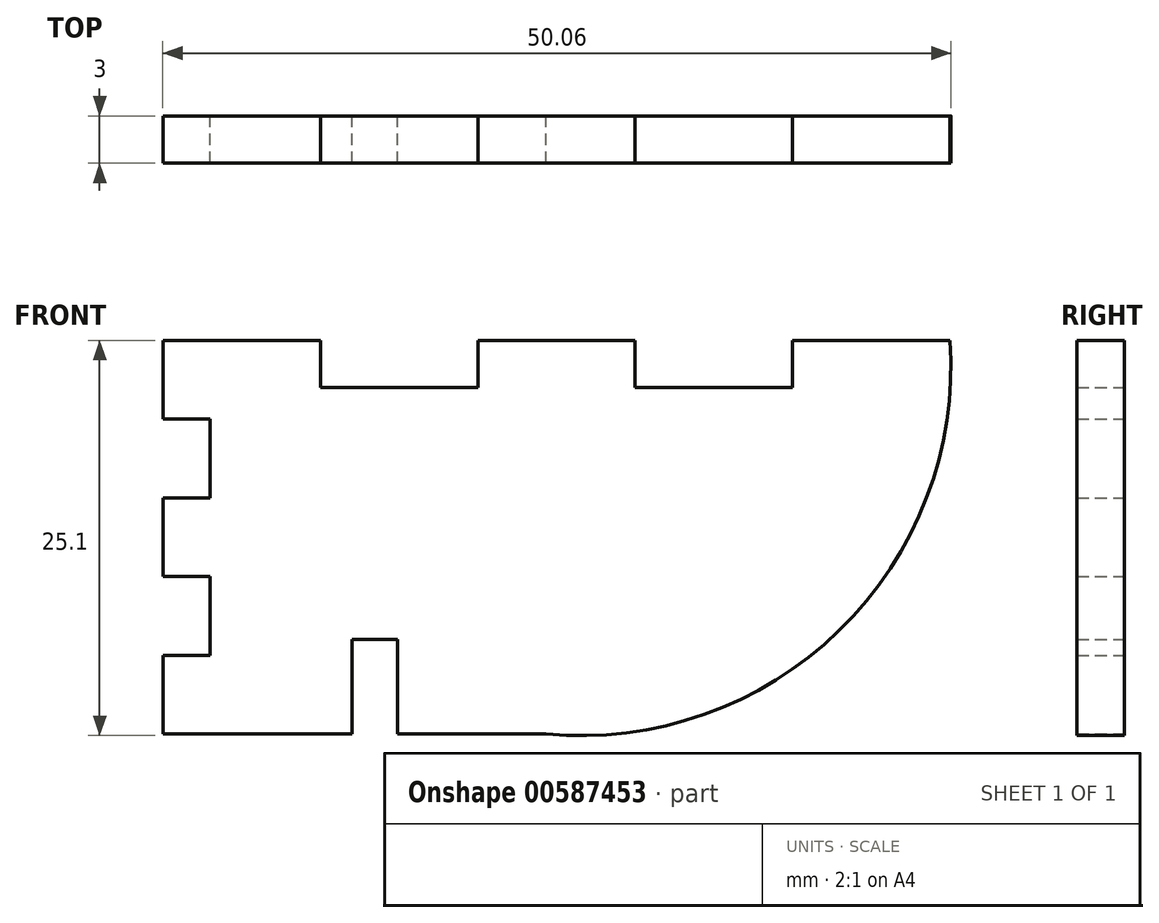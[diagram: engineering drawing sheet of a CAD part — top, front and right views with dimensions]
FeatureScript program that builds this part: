
annotation { "Feature Type Name" : "Feature", "Feature Type Description" : "" }
export const myFeature = defineFeature(function(context is Context, id is Id, definition is map)
    precondition{}
    {
        {
            var Q0;
            Q0=qCreatedBy(makeId("Front.planeOp"),FACE);
            var sketch = newSketch(context, id + "F0", { "sketchPlane" : qUnion([Q0])});
            skLineSegment(sketch, "E0", {"start": v(-35.85, 20) * mm, "end": v(-35.85, -5) * mm, "construction": true});
            skArc(sketch, "E1", {"start": v(-11.5, -5) * mm, "mid": v(7.1, 1.56) * mm, "end": v(14.15, 20) * mm});
            skLineSegment(sketch, "E2", {"start": v(-23.85, -5) * mm, "end": v(-23.85, 1) * mm});
            skLineSegment(sketch, "E3", {"start": v(-23.85, 1) * mm, "end": v(-20.95, 1) * mm});
            skLineSegment(sketch, "E4", {"start": v(-20.95, 1) * mm, "end": v(-20.95, -5) * mm});
            skLineSegment(sketch, "E5", {"start": v(-20.95, -5) * mm, "end": v(-11.5, -5) * mm});
            skLineSegment(sketch, "E6", {"start": v(-23.85, -5) * mm, "end": v(-35.85, -5) * mm});
            skLineSegment(sketch, "E7", {"start": v(-35.85, 0) * mm, "end": v(-32.85, 0) * mm});
            skLineSegment(sketch, "E8", {"start": v(-32.85, 0) * mm, "end": v(-32.85, 5) * mm});
            skLineSegment(sketch, "E9", {"start": v(-32.85, 5) * mm, "end": v(-35.85, 5) * mm});
            skLineSegment(sketch, "E10", {"start": v(-35.85, 5) * mm, "end": v(-35.85, 10) * mm});
            skLineSegment(sketch, "E11", {"start": v(-35.85, 10) * mm, "end": v(-32.85, 10) * mm});
            skLineSegment(sketch, "E12", {"start": v(-32.85, 10) * mm, "end": v(-32.85, 15) * mm});
            skLineSegment(sketch, "E13", {"start": v(-32.85, 15) * mm, "end": v(-35.85, 15) * mm});
            skLineSegment(sketch, "E14", {"start": v(-35.85, 15) * mm, "end": v(-35.85, 20) * mm});
            skLineSegment(sketch, "E15", {"start": v(-35.85, 0) * mm, "end": v(-35.85, -5) * mm});
            skLineSegment(sketch, "E16", {"start": v(-35.85, 20) * mm, "end": v(-25.85, 20) * mm});
            skLineSegment(sketch, "E17", {"start": v(-25.85, 20) * mm, "end": v(-25.85, 17) * mm});
            skLineSegment(sketch, "E18", {"start": v(-25.85, 17) * mm, "end": v(-15.85, 17) * mm});
            skLineSegment(sketch, "E19", {"start": v(-15.85, 17) * mm, "end": v(-15.85, 20) * mm});
            skLineSegment(sketch, "E20", {"start": v(-15.85, 20) * mm, "end": v(-5.85, 20) * mm});
            skLineSegment(sketch, "E21", {"start": v(-5.85, 20) * mm, "end": v(-5.85, 17) * mm});
            skLineSegment(sketch, "E22", {"start": v(-5.85, 17) * mm, "end": v(4.15, 17) * mm});
            skLineSegment(sketch, "E23", {"start": v(4.15, 17) * mm, "end": v(4.15, 20) * mm});
            skLineSegment(sketch, "E24", {"start": v(4.15, 20) * mm, "end": v(14.15, 20) * mm});
            skSolve(sketch);
        }
        {
            var Q0;
            Q0 = qSketchRegion(id + "F0", true);
            extrude(context, id + "F1", {"entities" : qUnion([Q0]), "depth" : 3 * mm, "offsetDistance" : 25 * mm});
        }
    });
